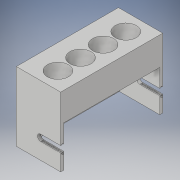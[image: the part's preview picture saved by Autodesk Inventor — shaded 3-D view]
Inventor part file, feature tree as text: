
AUTODESK INVENTOR PART (.ipt)
format: ipt  version: 2018 (Build 220112000, 112)  size: 322,560 bytes
history: native  units: in
note: dims shown in document units (in); Inventor stores cm internally (conversion verified against a paired STEP export)
features: extrude x16, sketch x15, projected_geometry x9, mirror x2, plane x1
ambient origin geometry x8: Origin, YZ Plane, XZ Plane, XY Plane, X Axis, Y Axis, Z Axis, Center Point
bodies: Solid1 (feature_tree)
feature tree (43):
  extrude  "Extrusion1"  Depth=9.0in
  extrude  "Extrusion2"  Depth=15.7in
  extrude  "Extrusion3"  Depth=0.5in
  extrude  "Extrusion4"  Depth=0.5in TaperAngle=0.0deg
  extrude  "Extrusion5"  Depth=1.05in
  extrude  "Extrusion6"  Depth=18.0in TaperAngle=0.0deg
  extrude  "Extrusion7"  Depth=3.25in
  extrude  "Extrusion11"  Depth=3.45in
  extrude  "Extrusion12"  Depth=3.25in
  plane  "Work Plane1"
  mirror  "Mirror1"
  extrude  "Extrusion14"  Depth=2.1in TaperAngle=0.0deg
  extrude  "Extrusion15"  Depth=0.75in TaperAngle=0.0deg
  extrude  "Extrusion16"  Depth=0.75in
  extrude  "Extrusion17"  Depth=0.75in
  mirror  "Mirror2"
  extrude  "Extrusion8"  Depth=4.95in
  extrude  "Extrusion9"  Depth=0.22in
  extrude  "Extrusion10"  Depth=4.0in TaperAngle=0.0deg
  sketch  "Sketch1"  dims[d0=16.7in d1=9.0in]
  sketch  "Sketch2"  dims[d2=6.5in d3=0.0in d4=15.7in]
  sketch  "Sketch4"  dims[d5=6.5in d6=0.5in]
  projected_geometry  "Projected Loop1"
  sketch  "Sketch5"  dims[d7=0.5in d8=5.85in d9=0.0in]
  projected_geometry  "Projected Loop2"
  sketch  "Sketch7"  dims[d10=3.775in d11=1.05in]
  projected_geometry  "Projected Loop4"
  sketch  "Sketch8"  dims[d12=2.475in d13=18.0in d14=0.0in]
  projected_geometry  "Projected Loop5"
  sketch  "Sketch9"  dims[d15=3.45in d16=3.25in]
  projected_geometry  "Projected Loop6"
  sketch  "Sketch10"  dims[d17=2.3in d18=3.45in]
  projected_geometry  "Projected Loop7"
  sketch  "Sketch11"  dims[d19=3.7in d20=3.25in]
  sketch  "Sketch12"  dims[d21=3.0in d22=0.0in d23=2.1in d24=0.0in]
  projected_geometry  "Projected Loop8"
  sketch  "Sketch13"  dims[d25=0.75in d26=0.0in d27=0.75in d28=0.0in]
  projected_geometry  "Projected Loop9"
  sketch  "Sketch15"  dims[d29=0.75in d30=0.75in]
  sketch  "Sketch17"  dims[d31=0.75in d32=0.75in]
  sketch  "Sketch18"  dims[d33=4.95in d34=4.95in]
  sketch  "Sketch19"  dims[d35=4.95in d36=4.95in d37=4.0in d38=0.0in d39=0.0in d40=1.5in d41=0.0in d42=1.5in d43=0.0in d44=0.22in d45=0.12in d46=0.14in d47=3.25in d48=0.0in d49=0.2in d50=0.0in d55=0.22in d56=0.075in d57=0.15in d58=0.0in d60=0.15in d61=0.04in d62=1.0in d63=0.0in d64=0.075in d65=0.081in d66=0.22in d67=0.0in d68=0.06in d69=0.0in]
  projected_geometry  "Projected Loop10"
